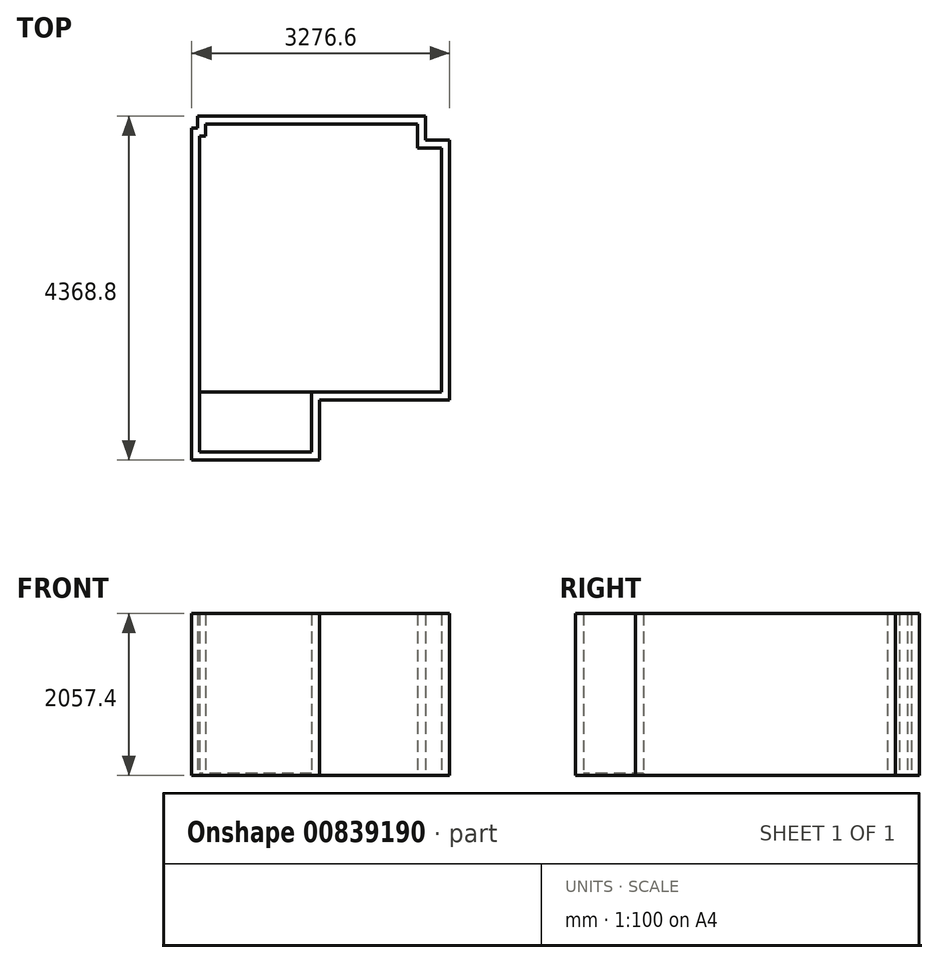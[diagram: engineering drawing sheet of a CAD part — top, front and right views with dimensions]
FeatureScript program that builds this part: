
annotation { "Feature Type Name" : "Feature", "Feature Type Description" : "" }
export const myFeature = defineFeature(function(context is Context, id is Id, definition is map)
    precondition{}
    {
        {
            var Q0;
            Q0=qCreatedBy(makeId("Top.planeOp"),FACE);
            var sketch = newSketch(context, id + "F0", { "sketchPlane" : qUnion([Q0])});
            skLineSegment(sketch, "E0.bottom", {"start": v(1536.7, -1701.8) * mm, "end": v(-1536.7, -1701.8) * mm});
            skLineSegment(sketch, "E0.top", {"start": v(1536.7, 1701.8) * mm, "end": v(-1536.7, 1701.8) * mm});
            skLineSegment(sketch, "E0.left", {"start": v(1536.7, -1701.8) * mm, "end": v(1536.7, 1701.8) * mm});
            skLineSegment(sketch, "E0.right", {"start": v(-1536.7, -1701.8) * mm, "end": v(-1536.7, 1701.8) * mm});
            skPoint(sketch, "E0.middle", {"position": v(0, 0) * mm});
            skLineSegment(sketch, "E1.bottom", {"start": v(-1536.7, -1701.8) * mm, "end": v(-114.3, -1701.8) * mm});
            skLineSegment(sketch, "E1.top", {"start": v(-1536.7, -2463.8) * mm, "end": v(-114.3, -2463.8) * mm});
            skLineSegment(sketch, "E1.left", {"start": v(-1536.7, -1701.8) * mm, "end": v(-1536.7, -2463.8) * mm});
            skLineSegment(sketch, "E1.right", {"start": v(-114.3, -1701.8) * mm, "end": v(-114.3, -2463.8) * mm});
            skLineSegment(sketch, "E2.bottom", {"start": v(-1536.7, 1701.8) * mm, "end": v(-1460.5, 1701.8) * mm});
            skLineSegment(sketch, "E2.top", {"start": v(-1536.7, 1549.4) * mm, "end": v(-1460.5, 1549.4) * mm});
            skLineSegment(sketch, "E2.left", {"start": v(-1536.7, 1701.8) * mm, "end": v(-1536.7, 1549.4) * mm});
            skLineSegment(sketch, "E2.right", {"start": v(-1460.5, 1701.8) * mm, "end": v(-1460.5, 1549.4) * mm});
            skLineSegment(sketch, "E3.bottom", {"start": v(1536.7, 1701.8) * mm, "end": v(1231.9, 1701.8) * mm});
            skLineSegment(sketch, "E3.top", {"start": v(1536.7, 1397) * mm, "end": v(1231.9, 1397) * mm});
            skLineSegment(sketch, "E3.left", {"start": v(1536.7, 1701.8) * mm, "end": v(1536.7, 1397) * mm});
            skLineSegment(sketch, "E3.right", {"start": v(1231.9, 1701.8) * mm, "end": v(1231.9, 1397) * mm});
            skSolve(sketch);
        }
        {
            var Q0;
            Q0=makeQuery(id+"F0.imprint","IMPRINT",FACE,{"disambiguationData":[TD([[makeQuery(id+"F0.imprint","IMPRINT",EDGE,{"derivedFrom":sQuery(id+"F0.wireOp",EDGE,"E1.top")}),1.0]])]});
            var Q1;
            {var subQ7=sQuery(id+"F0.wireOp",EDGE,"E2.top");Q1=makeQuery(id+"F0.imprint","IMPRINT",FACE,{"disambiguationData":[TD([[makeQuery(id+"F0.imprint","IMPRINT",EDGE,{"derivedFrom":subQ7}),-1.0]])]});}
            extrude(context, id + "F1", {"entities" : qUnion([Q0, Q1]), "depth" : 25.4 * mm, "offsetDistance" : 25.4 * mm});
        }
        {
            var Q0;
            Q0=makeQuery(id+"F1.opExtrude","CAP_FACE",FACE,{"disambiguationData":[OSD([sQuery(id+"F0.wireOp",EDGE,"E0.bottom"),sQuery(id+"F0.wireOp",EDGE,"E0.top"),sQuery(id+"F0.wireOp",EDGE,"E0.left"),sQuery(id+"F0.wireOp",EDGE,"E0.right"),sQuery(id+"F0.wireOp",EDGE,"E1.top"),sQuery(id+"F0.wireOp",EDGE,"E1.left"),sQuery(id+"F0.wireOp",EDGE,"E1.right"),sQuery(id+"F0.wireOp",EDGE,"E2.top"),sQuery(id+"F0.wireOp",EDGE,"E2.right"),sQuery(id+"F0.wireOp",EDGE,"E3.top"),sQuery(id+"F0.wireOp",EDGE,"E3.right")])],"isStart":false});
            var sketch = newSketch(context, id + "F2", { "sketchPlane" : qUnion([Q0])});
            skLineSegment(sketch, "E4.0", {"start": v(-1638.3, 1651) * mm, "end": v(-1562.1, 1651) * mm});
            skLineSegment(sketch, "E4.1", {"start": v(-1562.1, 1803.4) * mm, "end": v(-1562.1, 1651) * mm});
            skLineSegment(sketch, "E4.2", {"start": v(-1638.3, 1651) * mm, "end": v(-1638.3, -2565.4) * mm});
            skLineSegment(sketch, "E4.3", {"start": v(1333.5, 1803.4) * mm, "end": v(-1562.1, 1803.4) * mm});
            skLineSegment(sketch, "E4.4", {"start": v(1333.5, 1803.4) * mm, "end": v(1333.5, 1498.6) * mm});
            skLineSegment(sketch, "E4.5", {"start": v(1638.3, 1498.6) * mm, "end": v(1333.5, 1498.6) * mm});
            skLineSegment(sketch, "E4.6", {"start": v(-1638.3, -2565.4) * mm, "end": v(-12.7, -2565.4) * mm});
            skLineSegment(sketch, "E4.7", {"start": v(-12.7, -1803.4) * mm, "end": v(-12.7, -2565.4) * mm});
            skLineSegment(sketch, "E4.8", {"start": v(1638.3, -1803.4) * mm, "end": v(-12.7, -1803.4) * mm});
            skLineSegment(sketch, "E4.9", {"start": v(1638.3, -1803.4) * mm, "end": v(1638.3, 1498.6) * mm});
            skLineSegment(sketch, "E5.0.0", {"start": v(-114.3, -2463.8) * mm, "end": v(-114.3, -1701.8) * mm});
            skLineSegment(sketch, "E5.0.1", {"start": v(-114.3, -1701.8) * mm, "end": v(1536.7, -1701.8) * mm});
            skLineSegment(sketch, "E5.0.2", {"start": v(1536.7, -1701.8) * mm, "end": v(1536.7, 1397) * mm});
            skLineSegment(sketch, "E5.0.3", {"start": v(1536.7, 1397) * mm, "end": v(1231.9, 1397) * mm});
            skLineSegment(sketch, "E5.0.4", {"start": v(1231.9, 1397) * mm, "end": v(1231.9, 1701.8) * mm});
            skLineSegment(sketch, "E5.0.5", {"start": v(1231.9, 1701.8) * mm, "end": v(-1460.5, 1701.8) * mm});
            skLineSegment(sketch, "E5.0.6", {"start": v(-1460.5, 1701.8) * mm, "end": v(-1460.5, 1549.4) * mm});
            skLineSegment(sketch, "E5.0.7", {"start": v(-1460.5, 1549.4) * mm, "end": v(-1536.7, 1549.4) * mm});
            skLineSegment(sketch, "E5.0.8", {"start": v(-1536.7, 1549.4) * mm, "end": v(-1536.7, -2463.8) * mm});
            skLineSegment(sketch, "E5.0.9", {"start": v(-1536.7, -2463.8) * mm, "end": v(-114.3, -2463.8) * mm});
            skSolve(sketch);
        }
        {
            var Q0;
            Q0 = qSketchRegion(id + "F2", true);
            extrude(context, id + "F3", {"entities" : qUnion([Q0]), "operationType" : NewBodyOperationType.ADD, "depth" : 2032 * mm, "offsetDistance" : 25.4 * mm, "hasSecondDirection" : true, "secondDirectionOppositeDirection" : true, "secondDirectionDepth" : 25.4 * mm});
        }
    });
